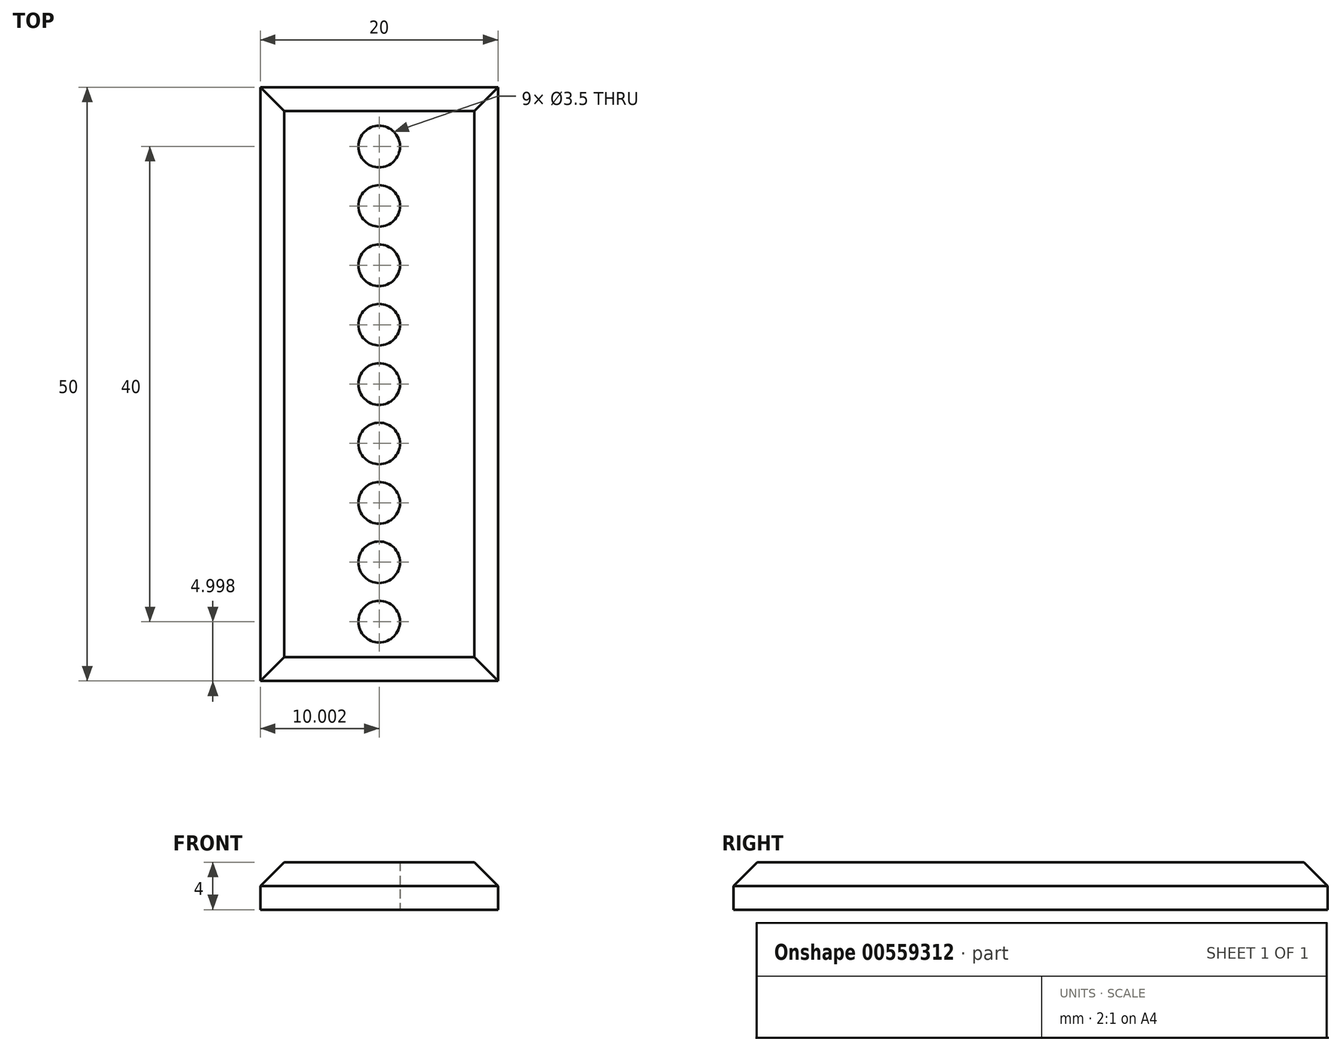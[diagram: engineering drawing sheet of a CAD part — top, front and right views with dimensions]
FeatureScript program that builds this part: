
annotation { "Feature Type Name" : "Feature", "Feature Type Description" : "" }
export const myFeature = defineFeature(function(context is Context, id is Id, definition is map)
    precondition{}
    {
        {
            var Q0;
            Q0=qCreatedBy(makeId("Top.planeOp"),FACE);
            var sketch = newSketch(context, id + "F0", { "sketchPlane" : qUnion([Q0])});
            skLineSegment(sketch, "E0.bottom", {"start": v(-15.63, 24.5) * mm, "end": v(4.37, 24.5) * mm});
            skLineSegment(sketch, "E0.top", {"start": v(-15.63, -25.5) * mm, "end": v(4.37, -25.5) * mm});
            skLineSegment(sketch, "E0.left", {"start": v(-15.63, 24.5) * mm, "end": v(-15.63, -25.5) * mm});
            skLineSegment(sketch, "E0.right", {"start": v(4.37, 24.5) * mm, "end": v(4.37, -25.5) * mm});
            skLineSegment(sketch, "E1", {"start": v(-5.63, 24.5) * mm, "end": v(-5.63, 19.5) * mm});
            skLineSegment(sketch, "E2", {"start": v(-5.63, 19.5) * mm, "end": v(-5.63, 14.5) * mm, "construction": true});
            skLineSegment(sketch, "E3", {"start": v(-5.63, 14.5) * mm, "end": v(-5.63, 9.5) * mm, "construction": true});
            skLineSegment(sketch, "E4", {"start": v(-5.63, 9.5) * mm, "end": v(-5.63, 4.5) * mm, "construction": true});
            skLineSegment(sketch, "E5", {"start": v(-5.63, 4.5) * mm, "end": v(-5.63, -0.5) * mm, "construction": true});
            skLineSegment(sketch, "E6", {"start": v(-5.63, -0.5) * mm, "end": v(-5.63, -5.5) * mm, "construction": true});
            skLineSegment(sketch, "E7", {"start": v(-5.63, -5.5) * mm, "end": v(-5.63, -10.5) * mm, "construction": true});
            skLineSegment(sketch, "E8", {"start": v(-5.63, -10.5) * mm, "end": v(-5.63, -15.5) * mm, "construction": true});
            skLineSegment(sketch, "E9", {"start": v(-5.63, -15.5) * mm, "end": v(-5.63, -20.5) * mm, "construction": true});
            skLineSegment(sketch, "E10", {"start": v(-5.63, -20.5) * mm, "end": v(-5.63, -25.5) * mm});
            skCircle(sketch, "E11", {"center": v(-5.63, 19.5) * mm, "radius": 1.75 * mm});
            skCircle(sketch, "E12", {"center": v(-5.63, 14.5) * mm, "radius": 1.75 * mm});
            skCircle(sketch, "E13", {"center": v(-5.63, 9.5) * mm, "radius": 1.75 * mm});
            skCircle(sketch, "E14", {"center": v(-5.63, 4.5) * mm, "radius": 1.75 * mm});
            skCircle(sketch, "E15", {"center": v(-5.63, -0.5) * mm, "radius": 1.75 * mm});
            skCircle(sketch, "E16", {"center": v(-5.63, -5.5) * mm, "radius": 1.75 * mm});
            skCircle(sketch, "E17", {"center": v(-5.63, -10.5) * mm, "radius": 1.75 * mm});
            skCircle(sketch, "E18", {"center": v(-5.63, -15.5) * mm, "radius": 1.75 * mm});
            skCircle(sketch, "E19", {"center": v(-5.63, -20.5) * mm, "radius": 1.75 * mm});
            skSolve(sketch);
        }
        {
            var Q0;
            {var subQ1=sQuery(id+"F0.wireOp",EDGE,"E0.left");Q0=makeQuery(id+"F0.imprint","IMPRINT",FACE,{"disambiguationData":[TD([[makeQuery(id+"F0.imprint","IMPRINT",EDGE,{"derivedFrom":subQ1}),1.0]])]});}
            extrude(context, id + "F1", {"entities" : qUnion([Q0]), "depth" : 4 * mm, "offsetDistance" : 25 * mm});
        }
        {
            var Q0;
            Q0=makeQuery(id+"F1.opExtrude","CAP_EDGE",EDGE,{"disambiguationData":[OSD([sQuery(id+"F0.wireOp",EDGE,"E0.left")])],"isStart":false});
            var Q1;
            Q1=makeQuery(id+"F1.opExtrude","CAP_EDGE",EDGE,{"disambiguationData":[OSD([sQuery(id+"F0.wireOp",EDGE,"E0.top")])],"isStart":false});
            var Q2;
            Q2=makeQuery(id+"F1.opExtrude","CAP_EDGE",EDGE,{"disambiguationData":[OSD([sQuery(id+"F0.wireOp",EDGE,"E0.right")])],"isStart":false});
            var Q3;
            Q3=makeQuery(id+"F1.opExtrude","CAP_EDGE",EDGE,{"disambiguationData":[OSD([sQuery(id+"F0.wireOp",EDGE,"E0.bottom")])],"isStart":false});
            chamfer(context, id + "F2", {"entities" : qUnion([Q0, Q1, Q2, Q3]), "width" : 2 * mm, "tangentPropagation" : true});
        }
    });
